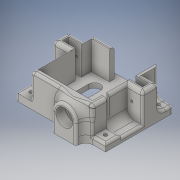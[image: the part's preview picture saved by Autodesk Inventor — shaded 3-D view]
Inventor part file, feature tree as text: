
AUTODESK INVENTOR PART (.ipt)
format: ipt  version: 2016 (Build 200138000, 138)  size: 498,176 bytes
history: native  units: in
note: dims shown in document units (in); Inventor stores cm internally (conversion verified against a paired STEP export)
features: sketch x8, extrude x7, fillet x5, hole x2
ambient origin geometry x8: Origin, YZ Plane, XZ Plane, XY Plane, X Axis, Y Axis, Z Axis, Center Point
bodies: Solid1 (feature_tree)
feature tree (22):
  extrude  "Extrusion1"  Depth=1.0433in
  sketch  "Sketch2"  dims[d2=0.0787in d3=0.0in]
  extrude  "Extrusion2"  TaperAngle=0.0deg  [1 undecoded]
  extrude  "Extrusion3"  Depth=0.4724in TaperAngle=0.0deg
  extrude  "Extrusion4"  Depth=0.0906in TaperAngle=0.0deg
  extrude  "Extrusion5"  Depth=0.4016in
  hole  "Hole1"  [1 undecoded]
  extrude  "Extrusion6"  Depth=0.2559in
  hole  "Hole2"  [1 undecoded]
  fillet  "Fillet1"  Radius=0.0394in
  fillet  "Fillet2"  Radius=0.0394in
  fillet  "Fillet3"  Radius=0.2559in
  extrude  "Extrusion7"  Depth=0.2559in
  fillet  "Fillet4"  Radius=0.2559in
  fillet  "Fillet5"  Radius=0.0394in
  sketch  "Sketch1"  dims[d0=1.4921in d1=1.0433in]
  sketch  "Sketch3"  dims[d4=0.8858in d5=0.1063in d6=0.1063in d7=0.6142in d8=0.6142in d9=0.1654in d10=0.1654in d11=0.2992in d12=0.2165in d13=0.9016in d14=0.0787in d15=0.0787in d16=0.0787in d17=0.0787in d18=0.0787in d19=0.0787in d20=0.1693in d21=0.0787in d22=0.0394in d23=0.0394in d24=0.0394in d25=0.1575in d26=0.0787in d27=0.0787in d28=0.0394in d29=0.9016in d33=0.2165in d34=0.0787in d35=0.9016in d36=0.0in]
  sketch  "Sketch4"  dims[d37=0.0in d38=0.4724in d39=0.0in]
  sketch  "Sketch5"  dims[d40=0.1575in d41=0.0in d42=0.0906in d43=0.0in]
  sketch  "Sketch6"  dims[d44=0.2835in d45=0.4016in]
  sketch  "Sketch7"  dims[d47=0.2323in d48=0.1575in d49=0.0in]
  sketch  "Sketch8"  dims[d52=0.2717in d53=0.2559in d54=0.2559in d55=0.0394in d56=0.0394in d57=0.0394in d58=0.2362in d59=0.1575in d60=0.0787in d61=90.0deg d62=0.315in d63=0.8108in d64=0.2559in d65=0.2559in d66=0.2559in d67=0.0394in d68=0.0in d69=0.128in d70=0.128in d71=0.128in d72=0.128in d73=0.128in d74=0.128in d75=0.128in d76=0.128in d77=0.0591in d78=0.2362in d79=0.1575in d80=0.0787in d81=90.0deg d82=0.315in d83=0.8108in d84=0.1181in d85=0.1181in d86=0.0394in d87=0.2362in d88=0.1969in d89=0.2362in d90=0.1969in d91=0.1969in d92=0.1969in d93=0.1575in d94=0.0in d95=0.0591in d96=0.0512in]
note: 3 required parameter values undecoded (feature->parameter linkage not recoverable at this tier; creation-order binding heuristic only, values carry confidence <= 0.55)
